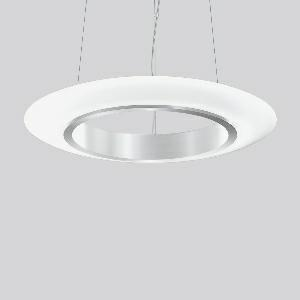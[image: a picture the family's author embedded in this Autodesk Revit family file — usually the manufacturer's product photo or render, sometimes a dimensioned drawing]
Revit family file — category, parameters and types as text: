
# Revit family: ring_of_fire_p_311570_004_76_9af4
name_source: partatom
category: Lighting Fixtures
units: mm (PartAtom-declared; Revit-internal decimal feet)

## family parameters
Cut with Voids When Loaded = No
Host = Face
Light Source = No
Part Type = Normal
Room Calculation Point = No
Round Connector Dimension = Use Diameter
Shared = No

## types (1)
- RING OF FIRE P (1 x LED Modul 830, 4050 lm, 3000)
    Apparent Load = 37 VA
    CIE Flux Codes = 43 73 90 55 100
    Color Rendering = 80
    Color Temperature = 3000
    Default Elevation = 1800 mm
    Description = Series: RING OF FIRE
A uniquely shaped pendant luminaire with elliptical glass. Supporting ring made of anodised aluminium. Canopy aluminium anodised. Opal glass: mouth-blown, satin finish. Suitable for pendant. 3-point steel cable suspension, steplessly adjustable. Special lengths available on request. For pendant lengths of up to 2 m, power is supplied through a suspension cable. For pendant lengths of 2 m and more, power must be supplied through a separate cable. Converter integrated in the canopy. TouchDim sensor capable. Light and/or presence sensors can be integrated. 
Colour: anodised aluminium
Diameter: 690 mm
Height: 81 mm
Suspension length: 500-1200 mm
Lamp: LED
Socket: without socket
Colour temperature: 3000K
Colour rendering index (CRI): 80
System power: 37 W
Rated luminous flux: 4050 lm
Luminous efficiency: 109 lm/W
Control gear: Converter, dimmable, DALI
Protection class: I
Type of protection: IP 20
    Height = 81 mm
    Lamp = 1 x LED Modul 830
    Lamp Light Flux = 4050 lm
    Lamp count = 1
    Length = 690 mm
    Lifetime = 50000 h
    Luminous efficacy = 109 lm/W
    Manufacturer = RZB
    ModVariant = No
    Model = 311570.004.76
    Mounting Place = Ceiling
    Mounting Type = Pendant
    Number of Poles = 1
    OnlyDefault = Yes
    Power Factor = 1
    Product Name = RING OF FIRE P
    Product group = Pendant luminaires
    ProductGroupID = 902
    Protection Class = Protection class I
    Protection Degree = IP 20
    RLX_Detail_Level = 1
    RLX_Emergency_Light_Flux = 0 lm
    RLX_Emergency_Type = 0
    RLX_Emergency_Type_DB = No
    RlxData = <blob elided: 30413 chars, md5=77acbec6>
    Socket = socket
    Standby Power = 0 W
    System Light Flux = 4050 lm
    System Power = 37 W
    Type Comments = Product without accessories
    Type Image = 311570.004.jpg
    URL = http://relux.com
    VarID = ---
    Voltage = 230 V
    Voltage Range = 220-240 V
    Weight = 0.00 kg
    Width = 0 mm  [stored 0 ft]

note: [stored X ft] marks values corroborated as IEEE doubles in the binary element streams (Revit-internal decimal feet)

## geometry (parser evidence)
native form markers: Blend x4, Sweep x12
no freeform markers — native parametric forms only
